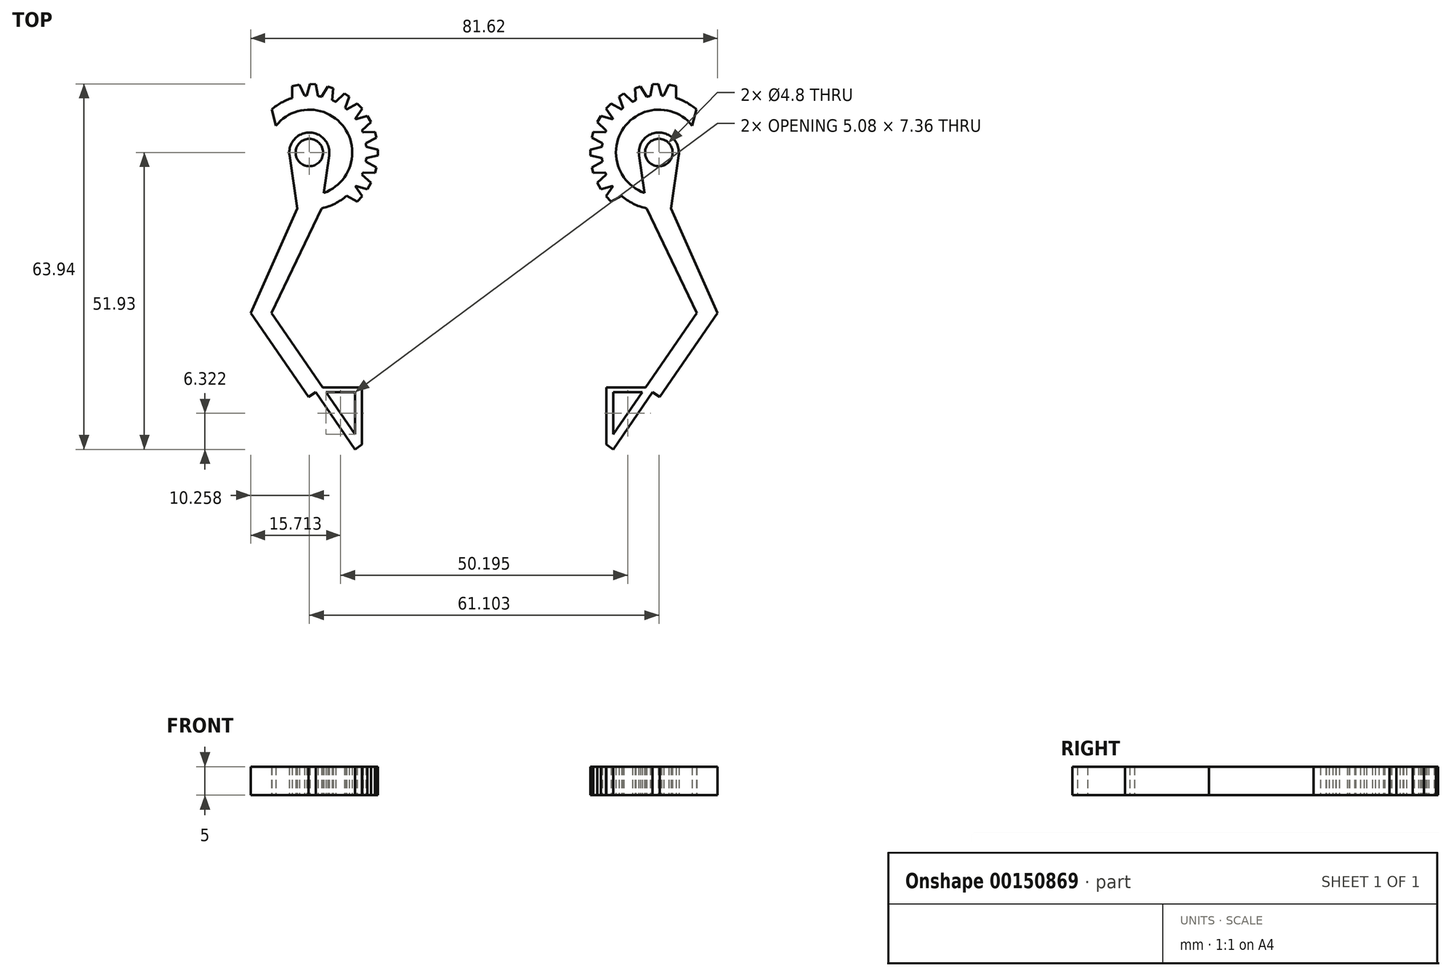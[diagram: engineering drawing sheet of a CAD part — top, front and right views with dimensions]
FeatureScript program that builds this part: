
annotation { "Feature Type Name" : "Feature", "Feature Type Description" : "" }
export const myFeature = defineFeature(function(context is Context, id is Id, definition is map)
    precondition{}
    {
        {
            var Q0;
            Q0=qCreatedBy(makeId("Top.planeOp"),FACE);
            var sketch = newSketch(context, id + "F0", { "sketchPlane" : qUnion([Q0])});
            skArc(sketch, "E0", {"start": v(-28.4, -9.77) * mm, "mid": v(-21.62, 4.49) * mm, "end": v(-37.1, 7.55) * mm});
            skLineSegment(sketch, "E1", {"start": v(-32.7, -9.77) * mm, "end": v(-40.8, -28.05) * mm});
            skLineSegment(sketch, "E2", {"start": v(-40.8, -28.05) * mm, "end": v(-30.7, -42.78) * mm});
            skLineSegment(sketch, "E3", {"start": v(-22.59, -51.93) * mm, "end": v(-21.35, -51.08) * mm});
            skLineSegment(sketch, "E4", {"start": v(-28.22, -41.08) * mm, "end": v(-37.17, -28.05) * mm});
            skLineSegment(sketch, "E5", {"start": v(-37.17, -28.05) * mm, "end": v(-28.4, -9.77) * mm});
            skLineSegment(sketch, "E6", {"start": v(-30.7, -42.78) * mm, "end": v(-28.22, -41.08) * mm});
            skArc(sketch, "E7", {"start": v(-28.02, -7.06) * mm, "mid": v(-24.44, 4.34) * mm, "end": v(-36.38, 4.72) * mm});
            skCircle(sketch, "E8", {"center": v(-30.55, 0) * mm, "radius": 3.5 * mm});
            skLineSegment(sketch, "E9", {"start": v(-32.7, -9.77) * mm, "end": v(-34.09, 0) * mm});
            skLineSegment(sketch, "E10", {"start": v(-28.4, -9.77) * mm, "end": v(-27.02, 0) * mm});
            skLineSegment(sketch, "E11.trimOffspring", {"start": v(-36.38, 4.72) * mm, "end": v(-37.1, 7.55) * mm});
            skCircle(sketch, "E12", {"center": v(-30.55, 0) * mm, "radius": 2.4 * mm});
            skLineSegment(sketch, "E13", {"start": v(-29.46, -41.93) * mm, "end": v(-22.59, -51.93) * mm});
            skPoint(sketch, "E14.orphan", {"position": v(-23.82, -52.78) * mm});
            skLineSegment(sketch, "E15", {"start": v(-21.35, -51.08) * mm, "end": v(-21.35, -41.08) * mm});
            skLineSegment(sketch, "E16", {"start": v(-21.35, -41.08) * mm, "end": v(-28.22, -41.08) * mm});
            skLineSegment(sketch, "E17", {"start": v(-22.56, -41.93) * mm, "end": v(-22.58, -49.29) * mm});
            skLineSegment(sketch, "E18", {"start": v(-28.22, -41.08) * mm, "end": v(-22.58, -49.29) * mm});
            skLineSegment(sketch, "E19", {"start": v(-27.64, -41.93) * mm, "end": v(-22.56, -41.93) * mm});
            skPoint(sketch, "E20.orphan", {"position": v(-21.35, -41.93) * mm});
            skLineSegment(sketch, "E21", {"start": v(-18.55, 0.5) * mm, "end": v(-20.6, 0.98) * mm});
            skLineSegment(sketch, "E22.MirrorCS", {"start": v(-18.55, -0.5) * mm, "end": v(-20.6, -0.98) * mm});
            skLineSegment(sketch, "E23", {"start": v(-18.55, 0.5) * mm, "end": v(-18.55, -0.5) * mm});
            skLineSegment(sketch, "E24.1.1", {"start": v(-18.83, -2.62) * mm, "end": v(-20.69, -1.63) * mm});
            skLineSegment(sketch, "E24.1.2", {"start": v(-18.83, -2.62) * mm, "end": v(-19.09, -3.59) * mm});
            skLineSegment(sketch, "E24.1.3", {"start": v(-19.09, -3.59) * mm, "end": v(-21.2, -3.52) * mm});
            skLineSegment(sketch, "E24.2.1", {"start": v(-19.8, -5.3) * mm, "end": v(-21.34, -3.87) * mm});
            skLineSegment(sketch, "E24.2.2", {"start": v(-19.8, -5.3) * mm, "end": v(-20.4, -6.43) * mm});
            skLineSegment(sketch, "E24.2.3", {"start": v(-20.4, -6.43) * mm, "end": v(-22.42, -5.83) * mm});
            skLineSegment(sketch, "E24.anchor1", {"start": v(-30.55, 0) * mm, "end": v(-20.6, -0.98) * mm, "construction": true});
            skLineSegment(sketch, "E24.anchor2", {"start": v(-30.55, 0) * mm, "end": v(-22.42, -5.83) * mm, "construction": true});
            skLineSegment(sketch, "E25.MirrorCS", {"start": v(-18.83, 2.62) * mm, "end": v(-20.69, 1.63) * mm});
            skLineSegment(sketch, "E26.MirrorCS", {"start": v(-19.09, 3.59) * mm, "end": v(-21.2, 3.52) * mm});
            skLineSegment(sketch, "E27.MirrorCS", {"start": v(-18.83, 2.62) * mm, "end": v(-19.09, 3.59) * mm});
            skLineSegment(sketch, "E28.MirrorCS", {"start": v(-19.8, 5.3) * mm, "end": v(-21.34, 3.87) * mm});
            skLineSegment(sketch, "E29.MirrorCS", {"start": v(-19.8, 5.3) * mm, "end": v(-20.4, 6.43) * mm});
            skLineSegment(sketch, "E30.MirrorCS", {"start": v(-20.4, 6.43) * mm, "end": v(-22.42, 5.83) * mm});
            skLineSegment(sketch, "E31.1.0", {"start": v(-33.54, 11.63) * mm, "end": v(-33.58, 9.53) * mm});
            skLineSegment(sketch, "E31.1.1", {"start": v(-32.28, 11.86) * mm, "end": v(-33.54, 11.63) * mm});
            skLineSegment(sketch, "E31.1.2", {"start": v(-32.28, 11.86) * mm, "end": v(-31.38, 9.96) * mm});
            skLineSegment(sketch, "E31.1.3", {"start": v(-30.42, 12) * mm, "end": v(-31.01, 9.99) * mm});
            skLineSegment(sketch, "E31.1.4", {"start": v(-29.42, 11.96) * mm, "end": v(-30.42, 12) * mm});
            skLineSegment(sketch, "E31.1.5", {"start": v(-29.42, 11.96) * mm, "end": v(-29.05, 9.89) * mm});
            skLineSegment(sketch, "E31.1.6", {"start": v(-24.44, 10.34) * mm, "end": v(-25.95, 8.88) * mm});
            skLineSegment(sketch, "E31.1.7", {"start": v(-23.6, 9.8) * mm, "end": v(-24.3, 7.81) * mm});
            skLineSegment(sketch, "E31.1.8", {"start": v(-24.44, 10.34) * mm, "end": v(-23.6, 9.8) * mm});
            skLineSegment(sketch, "E31.1.9", {"start": v(-22.18, 8.58) * mm, "end": v(-21.3, 7.66) * mm});
            skLineSegment(sketch, "E31.1.10", {"start": v(-21.3, 7.66) * mm, "end": v(-22.5, 5.93) * mm});
            skLineSegment(sketch, "E31.1.11", {"start": v(-22.18, 8.58) * mm, "end": v(-24.02, 7.57) * mm});
            skLineSegment(sketch, "E31.1.12", {"start": v(-26.37, 11.26) * mm, "end": v(-26.54, 9.16) * mm});
            skLineSegment(sketch, "E31.1.13", {"start": v(-27.32, 11.57) * mm, "end": v(-28.4, 9.77) * mm});
            skLineSegment(sketch, "E31.1.14", {"start": v(-27.32, 11.57) * mm, "end": v(-26.37, 11.26) * mm});
            skLineSegment(sketch, "E31.2.0", {"start": v(-42.54, 0.76) * mm, "end": v(-40.55, 0.06) * mm});
            skLineSegment(sketch, "E31.2.1", {"start": v(-42.37, 2.02) * mm, "end": v(-42.54, 0.76) * mm});
            skLineSegment(sketch, "E31.2.2", {"start": v(-42.37, 2.02) * mm, "end": v(-40.28, 2.29) * mm});
            skLineSegment(sketch, "E31.2.3", {"start": v(-41.93, 3.83) * mm, "end": v(-40.2, 2.65) * mm});
            skLineSegment(sketch, "E31.2.4", {"start": v(-41.58, 4.77) * mm, "end": v(-41.93, 3.83) * mm});
            skLineSegment(sketch, "E31.2.5", {"start": v(-41.58, 4.77) * mm, "end": v(-39.5, 4.48) * mm});
            skLineSegment(sketch, "E31.2.6", {"start": v(-38.5, 9.01) * mm, "end": v(-37.58, 7.12) * mm});
            skLineSegment(sketch, "E31.2.7", {"start": v(-37.71, 9.64) * mm, "end": v(-36.05, 8.35) * mm});
            skLineSegment(sketch, "E31.2.8", {"start": v(-38.5, 9.01) * mm, "end": v(-37.71, 9.64) * mm});
            skLineSegment(sketch, "E31.2.9", {"start": v(-36.13, 10.61) * mm, "end": v(-34.98, 11.17) * mm});
            skLineSegment(sketch, "E31.2.10", {"start": v(-34.98, 11.17) * mm, "end": v(-33.7, 9.5) * mm});
            skLineSegment(sketch, "E31.2.11", {"start": v(-36.13, 10.61) * mm, "end": v(-35.73, 8.55) * mm});
            skLineSegment(sketch, "E31.2.12", {"start": v(-39.97, 7.46) * mm, "end": v(-38.03, 6.64) * mm});
            skLineSegment(sketch, "E31.2.13", {"start": v(-40.55, 6.65) * mm, "end": v(-39.18, 5.06) * mm});
            skLineSegment(sketch, "E31.2.14", {"start": v(-40.55, 6.65) * mm, "end": v(-39.97, 7.46) * mm});
            skLineSegment(sketch, "E31.3.0", {"start": v(-34.98, -11.17) * mm, "end": v(-33.7, -9.5) * mm});
            skLineSegment(sketch, "E31.3.1", {"start": v(-36.13, -10.61) * mm, "end": v(-34.98, -11.17) * mm});
            skLineSegment(sketch, "E31.3.2", {"start": v(-36.13, -10.61) * mm, "end": v(-35.73, -8.55) * mm});
            skLineSegment(sketch, "E31.3.3", {"start": v(-37.71, -9.64) * mm, "end": v(-36.05, -8.35) * mm});
            skLineSegment(sketch, "E31.3.4", {"start": v(-38.5, -9.01) * mm, "end": v(-37.71, -9.64) * mm});
            skLineSegment(sketch, "E31.3.5", {"start": v(-38.5, -9.01) * mm, "end": v(-37.58, -7.12) * mm});
            skLineSegment(sketch, "E31.3.6", {"start": v(-41.58, -4.77) * mm, "end": v(-39.5, -4.48) * mm});
            skLineSegment(sketch, "E31.3.7", {"start": v(-41.93, -3.83) * mm, "end": v(-40.2, -2.65) * mm});
            skLineSegment(sketch, "E31.3.8", {"start": v(-41.58, -4.77) * mm, "end": v(-41.93, -3.83) * mm});
            skLineSegment(sketch, "E31.3.9", {"start": v(-42.37, -2.02) * mm, "end": v(-42.54, -0.76) * mm});
            skLineSegment(sketch, "E31.3.10", {"start": v(-42.54, -0.76) * mm, "end": v(-40.55, -0.06) * mm});
            skLineSegment(sketch, "E31.3.11", {"start": v(-42.37, -2.02) * mm, "end": v(-40.28, -2.29) * mm});
            skLineSegment(sketch, "E31.3.12", {"start": v(-40.55, -6.65) * mm, "end": v(-39.18, -5.06) * mm});
            skLineSegment(sketch, "E31.3.13", {"start": v(-39.97, -7.46) * mm, "end": v(-38.03, -6.64) * mm});
            skLineSegment(sketch, "E31.3.14", {"start": v(-39.97, -7.46) * mm, "end": v(-40.55, -6.65) * mm});
            skLineSegment(sketch, "E31.4.0", {"start": v(-21.3, -7.66) * mm, "end": v(-22.5, -5.93) * mm});
            skLineSegment(sketch, "E31.4.1", {"start": v(-22.18, -8.58) * mm, "end": v(-21.3, -7.66) * mm});
            skLineSegment(sketch, "E31.4.2", {"start": v(-22.18, -8.58) * mm, "end": v(-24.02, -7.57) * mm});
            skLineSegment(sketch, "E31.4.3", {"start": v(-23.6, -9.8) * mm, "end": v(-24.3, -7.81) * mm});
            skLineSegment(sketch, "E31.4.4", {"start": v(-24.44, -10.34) * mm, "end": v(-23.6, -9.8) * mm});
            skLineSegment(sketch, "E31.4.5", {"start": v(-24.44, -10.34) * mm, "end": v(-25.95, -8.88) * mm});
            skLineSegment(sketch, "E31.4.6", {"start": v(-29.42, -11.96) * mm, "end": v(-29.05, -9.89) * mm});
            skLineSegment(sketch, "E31.4.7", {"start": v(-30.42, -12) * mm, "end": v(-31.01, -9.99) * mm});
            skLineSegment(sketch, "E31.4.8", {"start": v(-29.42, -11.96) * mm, "end": v(-30.42, -12) * mm});
            skLineSegment(sketch, "E31.4.9", {"start": v(-32.28, -11.86) * mm, "end": v(-33.54, -11.63) * mm});
            skLineSegment(sketch, "E31.4.10", {"start": v(-33.54, -11.63) * mm, "end": v(-33.58, -9.53) * mm});
            skLineSegment(sketch, "E31.4.11", {"start": v(-32.28, -11.86) * mm, "end": v(-31.38, -9.96) * mm});
            skLineSegment(sketch, "E31.4.12", {"start": v(-27.32, -11.57) * mm, "end": v(-28.4, -9.77) * mm});
            skLineSegment(sketch, "E31.4.13", {"start": v(-26.37, -11.26) * mm, "end": v(-26.54, -9.16) * mm});
            skLineSegment(sketch, "E31.4.14", {"start": v(-26.37, -11.26) * mm, "end": v(-27.32, -11.57) * mm});
            skSolve(sketch);
        }
        {
            var Q0;
            {var subQ0=sQuery(id+"F0.wireOp",EDGE,"E0");Q0=makeQuery(id+"F0.imprint","IMPRINT",FACE,{"disambiguationData":[TD([[makeQuery(id+"F0.imprint","IMPRINT",EDGE,{"derivedFrom":subQ0}),1.0]])]});}
            var Q1;
            Q1=makeQuery(id+"F0.imprint","IMPRINT",FACE,{"disambiguationData":[TD([[makeQuery(id+"F0.imprint","IMPRINT",EDGE,{"derivedFrom":sQuery(id+"F0.wireOp",EDGE,"E12")}),-1.0]])]});
            var Q2;
            {var subQ9=sQuery(id+"F0.wireOp",EDGE,"E1");Q2=makeQuery(id+"F0.imprint","IMPRINT",FACE,{"disambiguationData":[TD([[makeQuery(id+"F0.imprint","IMPRINT",EDGE,{"derivedFrom":subQ9}),1.0]])]});}
            var Q3;
            Q3=makeQuery(id+"F0.imprint","IMPRINT",FACE,{"disambiguationData":[TD([[makeQuery(id+"F0.imprint","IMPRINT",EDGE,{"derivedFrom":sQuery(id+"F0.wireOp",EDGE,"E3")}),1.0]])]});
            var Q4;
            {var subQ0=sQuery(id+"F0.wireOp",EDGE,"bc312b0d-6e01-4dc7-9e0c-0af0b0e97ea60.MirrorCS");Q4=makeQuery(id+"F0.imprint","IMPRINT",FACE,{"disambiguationData":[TD([[makeQuery(id+"F0.imprint","IMPRINT",EDGE,{"derivedFrom":subQ0}),-1.0]])]});}
            var Q5;
            {var subQ0=sQuery(id+"F0.wireOp",EDGE,"462d524d-2b27-4872-b0f5-b4a3b8a689d10.MirrorCS");Q5=makeQuery(id+"F0.imprint","IMPRINT",FACE,{"disambiguationData":[TD([[makeQuery(id+"F0.imprint","IMPRINT",EDGE,{"derivedFrom":subQ0}),-1.0]])]});}
            var Q6;
            {var subQ1=sQuery(id+"F0.wireOp",EDGE,"E21");Q6=makeQuery(id+"F0.imprint","IMPRINT",FACE,{"disambiguationData":[TD([[makeQuery(id+"F0.imprint","IMPRINT",EDGE,{"derivedFrom":subQ1}),1.0]])]});}
            var Q7;
            {var subQ0=sQuery(id+"F0.wireOp",EDGE,"E24.1.1");Q7=makeQuery(id+"F0.imprint","IMPRINT",FACE,{"disambiguationData":[TD([[makeQuery(id+"F0.imprint","IMPRINT",EDGE,{"derivedFrom":subQ0}),1.0]])]});}
            var Q8;
            {var subQ0=sQuery(id+"F0.wireOp",EDGE,"E24.2.1");Q8=makeQuery(id+"F0.imprint","IMPRINT",FACE,{"disambiguationData":[TD([[makeQuery(id+"F0.imprint","IMPRINT",EDGE,{"derivedFrom":subQ0}),1.0]])]});}
            var Q9;
            {var subQ4=sQuery(id+"F0.wireOp",EDGE,"9bb37613-ee5e-4ddf-90ce-3e862456e0270.MirrorCS");Q9=makeQuery(id+"F0.imprint","IMPRINT",FACE,{"disambiguationData":[TD([[makeQuery(id+"F0.imprint","IMPRINT",EDGE,{"derivedFrom":subQ4}),1.0]])]});}
            var Q10;
            {var subQ0=sQuery(id+"F0.wireOp",EDGE,"cd796243-9807-4365-be5c-b11cb8aa61bb0.MirrorCS");Q10=makeQuery(id+"F0.imprint","IMPRINT",FACE,{"disambiguationData":[TD([[makeQuery(id+"F0.imprint","IMPRINT",EDGE,{"derivedFrom":subQ0}),-1.0]])]});}
            var Q11;
            {var subQ4=sQuery(id+"F0.wireOp",EDGE,"E29.MirrorCS");Q11=makeQuery(id+"F0.imprint","IMPRINT",FACE,{"disambiguationData":[TD([[makeQuery(id+"F0.imprint","IMPRINT",EDGE,{"derivedFrom":subQ4}),1.0]])]});}
            var Q12;
            {var subQ0=sQuery(id+"F0.wireOp",EDGE,"E25.MirrorCS");Q12=makeQuery(id+"F0.imprint","IMPRINT",FACE,{"disambiguationData":[TD([[makeQuery(id+"F0.imprint","IMPRINT",EDGE,{"derivedFrom":subQ0}),-1.0]])]});}
            extrude(context, id + "F1", {"entities" : qUnion([Q0, Q1, Q2, Q3, Q4, Q5, Q6, Q7, Q8, Q9, Q10, Q11, Q12]), "depth" : 5 * mm});
        }
        {
            var Q0;
            {var subQ0=sQuery(id+"F0.wireOp",EDGE,"E31.4.0");Q0=makeQuery(id+"F0.imprint","IMPRINT",FACE,{"disambiguationData":[TD([[makeQuery(id+"F0.imprint","IMPRINT",EDGE,{"derivedFrom":subQ0}),1.0]])]});}
            var Q1;
            {var subQ4=sQuery(id+"F0.wireOp",EDGE,"E31.1.9");Q1=makeQuery(id+"F0.imprint","IMPRINT",FACE,{"disambiguationData":[TD([[makeQuery(id+"F0.imprint","IMPRINT",EDGE,{"derivedFrom":subQ4}),-1.0]])]});}
            var Q2;
            {var subQ0=sQuery(id+"F0.wireOp",EDGE,"E31.1.6");Q2=makeQuery(id+"F0.imprint","IMPRINT",FACE,{"disambiguationData":[TD([[makeQuery(id+"F0.imprint","IMPRINT",EDGE,{"derivedFrom":subQ0}),1.0]])]});}
            var Q3;
            {var subQ0=sQuery(id+"F0.wireOp",EDGE,"E31.1.12");Q3=makeQuery(id+"F0.imprint","IMPRINT",FACE,{"disambiguationData":[TD([[makeQuery(id+"F0.imprint","IMPRINT",EDGE,{"derivedFrom":subQ0}),-1.0]])]});}
            var Q4;
            {var subQ0=sQuery(id+"F0.wireOp",EDGE,"E31.1.3");Q4=makeQuery(id+"F0.imprint","IMPRINT",FACE,{"disambiguationData":[TD([[makeQuery(id+"F0.imprint","IMPRINT",EDGE,{"derivedFrom":subQ0}),1.0]])]});}
            var Q5;
            {var subQ0=sQuery(id+"F0.wireOp",EDGE,"E31.1.0");Q5=makeQuery(id+"F0.imprint","IMPRINT",FACE,{"disambiguationData":[TD([[makeQuery(id+"F0.imprint","IMPRINT",EDGE,{"derivedFrom":subQ0}),1.0]])]});}
            extrude(context, id + "F2", {"entities" : qUnion([Q0, Q1, Q2, Q3, Q4, Q5]), "operationType" : NewBodyOperationType.ADD, "depth" : 5 * mm});
        }
        {
            var Q0;
            Q0=makeQuery(id+"F1.opExtrude","SWEPT_BODY",BODY,{"disambiguationData":[OSD([sQuery(id+"F0.wireOp",EDGE,"E0"),sQuery(id+"F0.wireOp",EDGE,"E1"),sQuery(id+"F0.wireOp",EDGE,"E2"),sQuery(id+"F0.wireOp",EDGE,"E3"),sQuery(id+"F0.wireOp",EDGE,"E4"),sQuery(id+"F0.wireOp",EDGE,"E5"),sQuery(id+"F0.wireOp",EDGE,"E6"),sQuery(id+"F0.wireOp",EDGE,"E7"),sQuery(id+"F0.wireOp",EDGE,"E8"),sQuery(id+"F0.wireOp",EDGE,"E9"),sQuery(id+"F0.wireOp",EDGE,"E10"),sQuery(id+"F0.wireOp",EDGE,"E11.trimOffspring"),sQuery(id+"F0.wireOp",EDGE,"E12"),sQuery(id+"F0.wireOp",EDGE,"E13"),sQuery(id+"F0.wireOp",EDGE,"E15"),sQuery(id+"F0.wireOp",EDGE,"E16"),sQuery(id+"F0.wireOp",EDGE,"E17"),sQuery(id+"F0.wireOp",EDGE,"E18"),sQuery(id+"F0.wireOp",EDGE,"E19"),sQuery(id+"F0.wireOp",EDGE,"E21"),sQuery(id+"F0.wireOp",EDGE,"E22.MirrorCS"),sQuery(id+"F0.wireOp",EDGE,"E23"),sQuery(id+"F0.wireOp",EDGE,"E24.1.1"),sQuery(id+"F0.wireOp",EDGE,"E24.1.2"),sQuery(id+"F0.wireOp",EDGE,"E24.1.3"),sQuery(id+"F0.wireOp",EDGE,"E24.2.1"),sQuery(id+"F0.wireOp",EDGE,"E24.2.2"),sQuery(id+"F0.wireOp",EDGE,"E24.2.3"),sQuery(id+"F0.wireOp",EDGE,"E25.MirrorCS"),sQuery(id+"F0.wireOp",EDGE,"E26.MirrorCS"),sQuery(id+"F0.wireOp",EDGE,"E27.MirrorCS"),sQuery(id+"F0.wireOp",EDGE,"E28.MirrorCS"),sQuery(id+"F0.wireOp",EDGE,"E29.MirrorCS"),sQuery(id+"F0.wireOp",EDGE,"E30.MirrorCS")])]});
            var Q1;
            Q1=qCreatedBy(makeId("Right.planeOp"),FACE);
            mirror(context, id + "F3", {"entities" : qUnion([Q0]), "mirrorPlane" : qUnion([Q1])});
        }
    });
